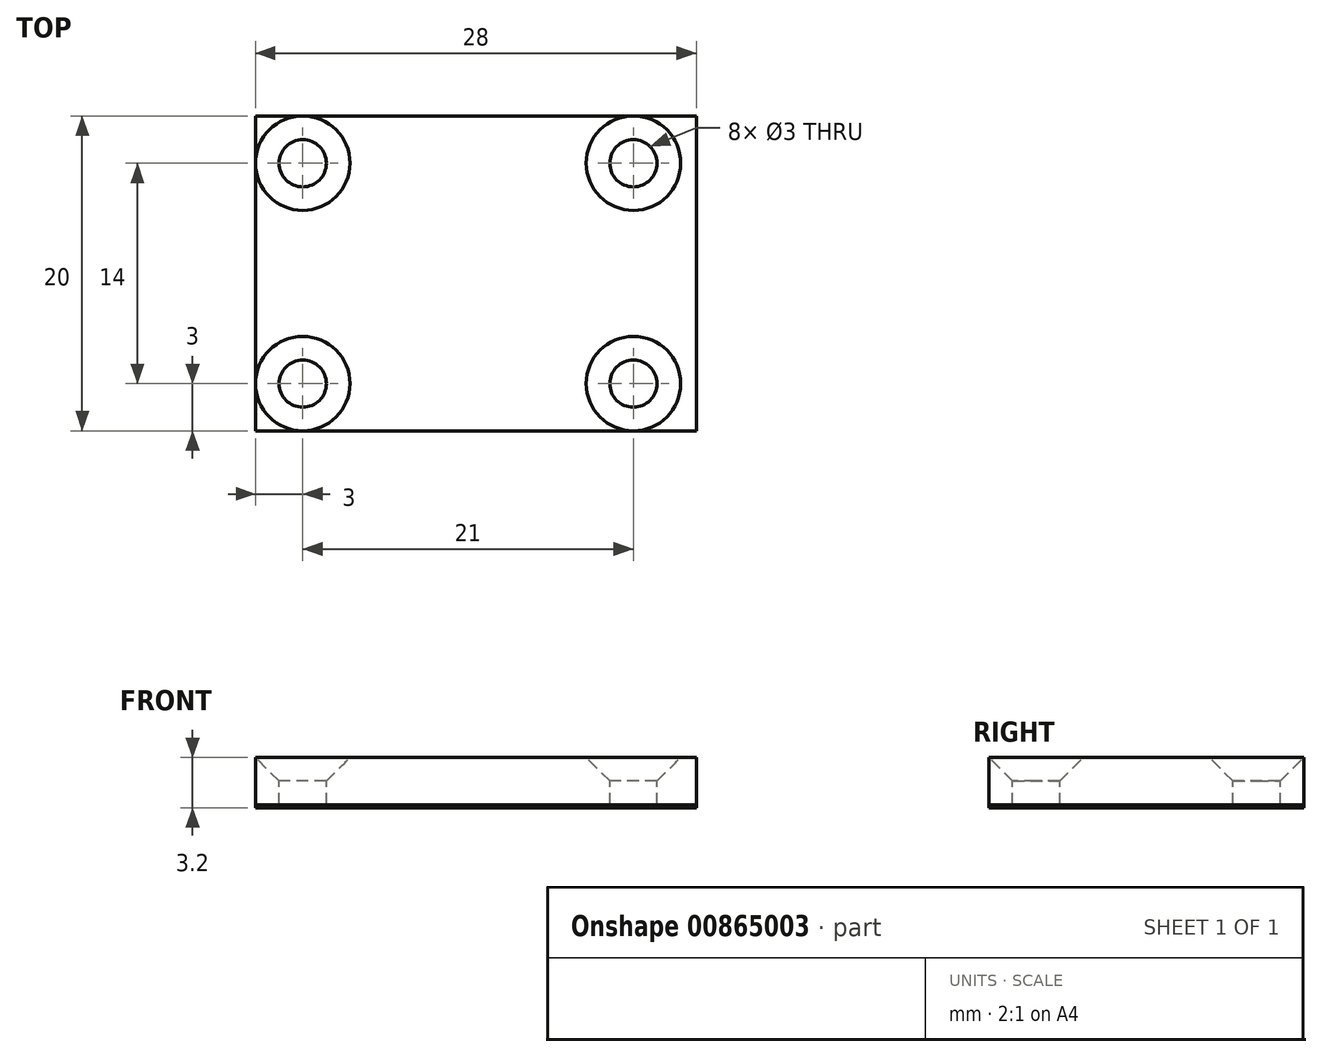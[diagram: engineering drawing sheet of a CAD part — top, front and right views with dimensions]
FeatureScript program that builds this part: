
annotation { "Feature Type Name" : "Feature", "Feature Type Description" : "" }
export const myFeature = defineFeature(function(context is Context, id is Id, definition is map)
    precondition{}
    {
        {
            var Q0;
            Q0=qCreatedBy(makeId("Top.planeOp"),FACE);
            var sketch = newSketch(context, id + "F0", { "sketchPlane" : qUnion([Q0])});
            skLineSegment(sketch, "E0.bottom", {"start": v(14, 0) * mm, "end": v(-14, 0) * mm});
            skLineSegment(sketch, "E0.top", {"start": v(14, 10) * mm, "end": v(-14, 10) * mm});
            skLineSegment(sketch, "E0.right", {"start": v(-14, 0) * mm, "end": v(-14, 10) * mm});
            skPoint(sketch, "E1", {"position": v(-11, 7) * mm});
            skLineSegment(sketch, "E2", {"start": v(14, 10) * mm, "end": v(14, 0) * mm});
            skPoint(sketch, "E3", {"position": v(10, 7) * mm});
            skSolve(sketch);
        }
        {
            var Q0;
            Q0=makeQuery(id+"F0.imprint","IMPRINT",FACE,{"disambiguationData":[TD([[makeQuery(id+"F0.imprint","IMPRINT",EDGE,{"derivedFrom":sQuery(id+"F0.wireOp",EDGE,"E0.bottom")}),-1.0]])]});
            extrude(context, id + "F1", {"entities" : qUnion([Q0]), "oppositeDirection" : true, "depth" : 3 * mm, "offsetDistance" : 25 * mm});
        }
        {
            var Q0;
            Q0=sQuery(id+"F0.wireOp",VERTEX,"E1");
            var Q1;
            Q1=sQuery(id+"F0.wireOp",VERTEX,"E3");
            var Q2;
            Q2=makeQuery(id+"F1.opExtrude","SWEPT_BODY",BODY,{"disambiguationData":[OSD([sQuery(id+"F0.wireOp",EDGE,"E0.bottom"),sQuery(id+"F0.wireOp",EDGE,"E0.top"),sQuery(id+"F0.wireOp",EDGE,"E0.left"),sQuery(id+"F0.wireOp",EDGE,"E0.right")])]});
            hole(context, id + "F2", {"style" : HoleStyle.C_SINK, "endStyle" : HoleEndStyle.BLIND, "holeDiameter" : 3 * mm, "cSinkDiameter" : 6 * mm, "cSinkAngle" : 90 * degree, "majorDiameter" : 4 * mm, "holeDepth" : 3 * mm, "isTappedThrough" : true, "tappedDepth" : 7.9 * mm, "tapClearance" : 3, "startFromSketch" : true, "locations" : qUnion([Q0, Q1]), "scope" : qUnion([Q2])});
        }
        {
            var Q0;
            Q0=makeQuery(id+"F1.opExtrude","SWEPT_BODY",BODY,{"disambiguationData":[OSD([sQuery(id+"F0.wireOp",EDGE,"E0.bottom"),sQuery(id+"F0.wireOp",EDGE,"E0.top"),sQuery(id+"F0.wireOp",EDGE,"E0.left"),sQuery(id+"F0.wireOp",EDGE,"E0.right")])]});
            var Q1;
            Q1=qCreatedBy(makeId("Front.planeOp"),FACE);
            mirror(context, id + "F3", {"operationType" : NewBodyOperationType.ADD, "entities" : qUnion([Q0]), "mirrorPlane" : qUnion([Q1])});
        }
        {
            var Q0;
            {var subQ0=makeQuery(id+"F1.opExtrude","CAP_FACE",FACE,{"disambiguationData":[OSD([sQuery(id+"F0.wireOp",EDGE,"E0.bottom"),sQuery(id+"F0.wireOp",EDGE,"E0.top"),sQuery(id+"F0.wireOp",EDGE,"E0.left"),sQuery(id+"F0.wireOp",EDGE,"E0.right")])],"isStart":false});var subQ1=makeQuery(id+"FEvW42HuMpM1IpE_1.boolean.opBoolean","MERGE",FACE,{"derivedFrom":[subQ0,makeQuery(id+"FEvW42HuMpM1IpE_1.opPattern","COPY",FACE,{"derivedFrom":subQ0,"instanceName":"1"})]});Q0=makeQuery(id+"F3.boolean.opBoolean","MERGE",FACE,{"derivedFrom":[subQ1,makeQuery(id+"F3.opPattern","COPY",FACE,{"derivedFrom":subQ1,"instanceName":"1"})]});}
            var sketch = newSketch(context, id + "F4", { "sketchPlane" : qUnion([Q0])});
            skLineSegment(sketch, "E4.0", {"start": v(14, 10) * mm, "end": v(-14, 10) * mm});
            skLineSegment(sketch, "E4.1", {"start": v(-14, 10) * mm, "end": v(-14, -10) * mm});
            skCircle(sketch, "E4.2", {"center": v(-11, 7) * mm, "radius": 1.5 * mm});
            skLineSegment(sketch, "E4.6", {"start": v(14, -10) * mm, "end": v(-14, -10) * mm});
            skCircle(sketch, "E4.7", {"center": v(-11, -7) * mm, "radius": 1.5 * mm});
            skCircle(sketch, "E5.0", {"center": v(10, 7) * mm, "radius": 1.5 * mm});
            skCircle(sketch, "E5.1", {"center": v(10, -7) * mm, "radius": 1.5 * mm});
            skLineSegment(sketch, "E5.2", {"start": v(14, -10) * mm, "end": v(14, 10) * mm});
            skSolve(sketch);
        }
        {
            var Q0;
            Q0 = qSketchRegion(id + "F4", true);
            extrude(context, id + "F5", {"entities" : qUnion([Q0]), "depth" : 0.2 * mm, "offsetDistance" : 25 * mm});
        }
    });
